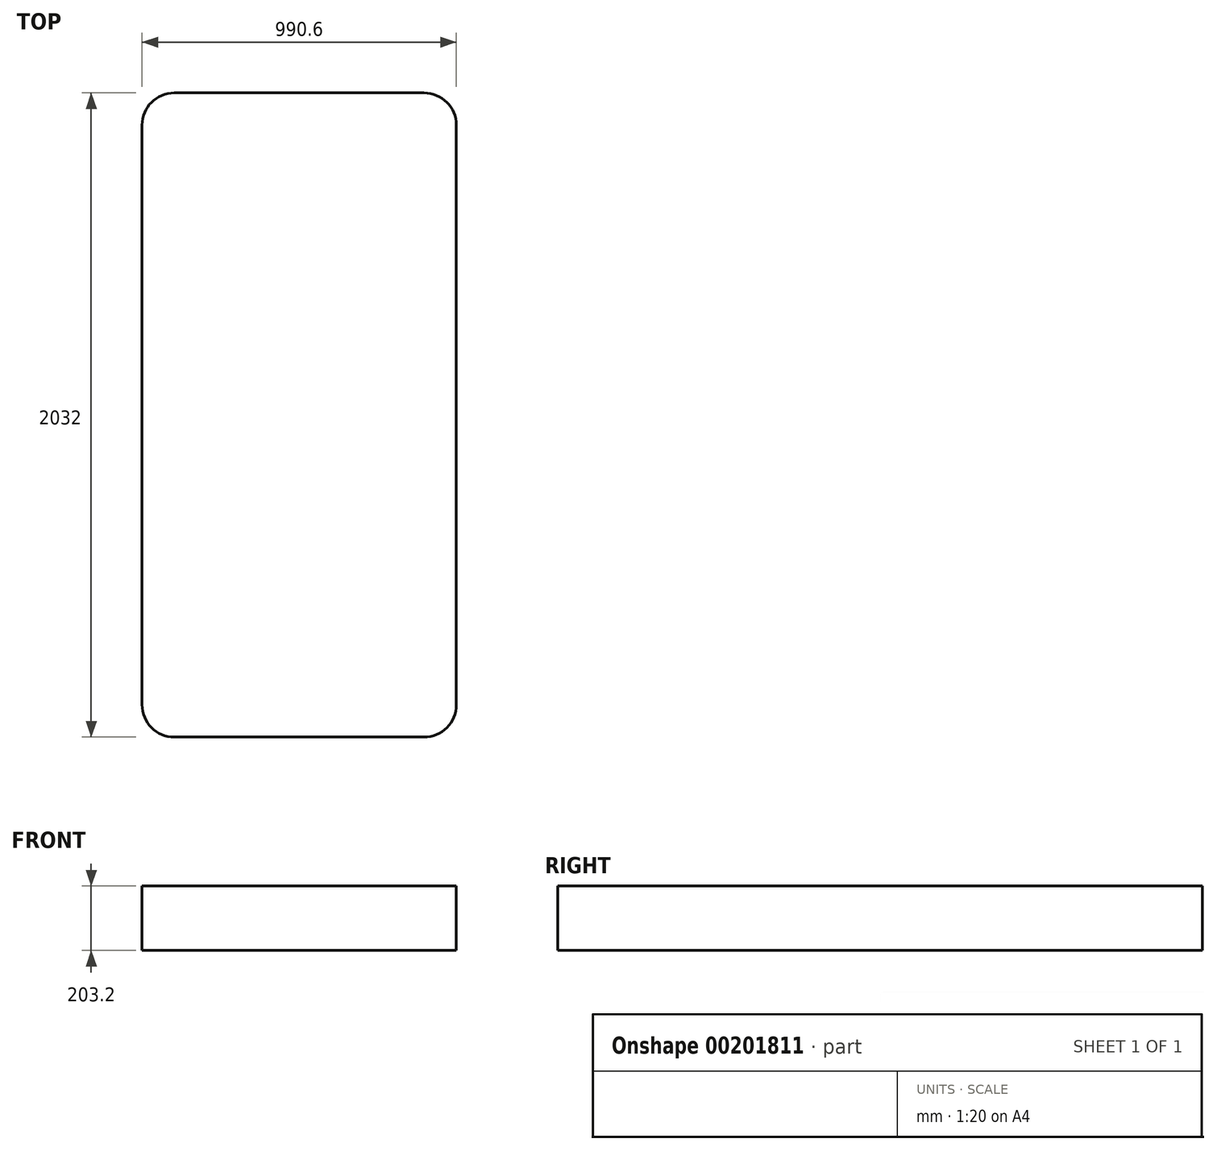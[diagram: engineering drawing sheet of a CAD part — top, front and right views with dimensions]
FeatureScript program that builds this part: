
annotation { "Feature Type Name" : "Feature", "Feature Type Description" : "" }
export const myFeature = defineFeature(function(context is Context, id is Id, definition is map)
    precondition{}
    {
        {
            var Q0;
            Q0=qCreatedBy(makeId("Top.planeOp"),FACE);
            var sketch = newSketch(context, id + "F0", { "sketchPlane" : qUnion([Q0])});
            skLineSegment(sketch, "E0.bottom", {"start": v(495.3, -1016) * mm, "end": v(-495.3, -1016) * mm});
            skLineSegment(sketch, "E0.top", {"start": v(495.3, 1016) * mm, "end": v(-495.3, 1016) * mm});
            skLineSegment(sketch, "E0.left", {"start": v(495.3, -1016) * mm, "end": v(495.3, 1016) * mm});
            skLineSegment(sketch, "E0.right", {"start": v(-495.3, -1016) * mm, "end": v(-495.3, 1016) * mm});
            skPoint(sketch, "E0.middle", {"position": v(0, 0) * mm});
            skSolve(sketch);
        }
        {
            var Q0;
            Q0 = qSketchRegion(id + "F0", true);
            extrude(context, id + "F1", {"entities" : qUnion([Q0]), "depth" : 203.2 * mm});
        }
        {
            var Q0;
            Q0=makeQuery(id+"F1.opExtrude","SWEPT_EDGE",EDGE,{"disambiguationData":[OSD([sQuery(id+"F0.wireOp",EDGE,"E0.bottom"),sQuery(id+"F0.wireOp",EDGE,"E0.right")])]});
            var Q1;
            Q1=makeQuery(id+"F1.opExtrude","SWEPT_EDGE",EDGE,{"disambiguationData":[OSD([sQuery(id+"F0.wireOp",EDGE,"E0.bottom"),sQuery(id+"F0.wireOp",EDGE,"E0.left")])]});
            var Q2;
            Q2=makeQuery(id+"F1.opExtrude","SWEPT_EDGE",EDGE,{"disambiguationData":[OSD([sQuery(id+"F0.wireOp",EDGE,"E0.top"),sQuery(id+"F0.wireOp",EDGE,"E0.right")])]});
            var Q3;
            Q3=makeQuery(id+"F1.opExtrude","SWEPT_EDGE",EDGE,{"disambiguationData":[OSD([sQuery(id+"F0.wireOp",EDGE,"E0.top"),sQuery(id+"F0.wireOp",EDGE,"E0.left")])]});
            fillet(context, id + "F2", {"entities" : qUnion([Q0, Q1, Q2, Q3]), "radius" : 101.6 * mm, "tangentPropagation" : true, "allowEdgeOverflow" : false});
        }
    });
